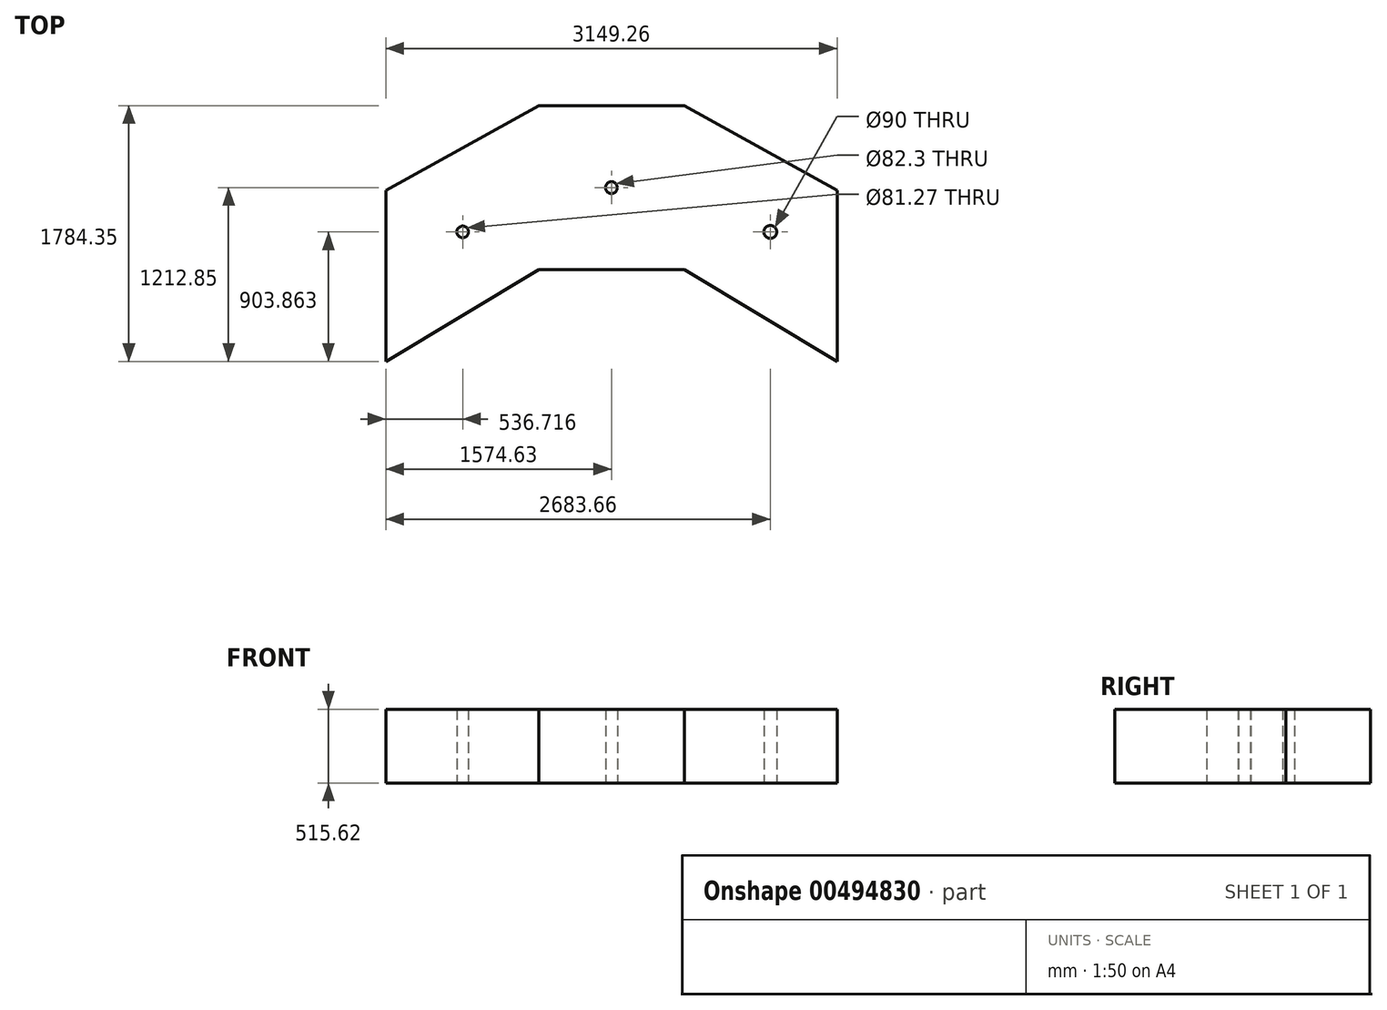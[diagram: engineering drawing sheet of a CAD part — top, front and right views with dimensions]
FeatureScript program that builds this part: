
annotation { "Feature Type Name" : "Feature", "Feature Type Description" : "" }
export const myFeature = defineFeature(function(context is Context, id is Id, definition is map)
    precondition{}
    {
        {
            var Q0;
            Q0=qCreatedBy(makeId("Top.planeOp"),FACE);
            var sketch = newSketch(context, id + "F0", { "sketchPlane" : qUnion([Q0])});
            skLineSegment(sketch, "E0", {"start": v(459.4, 1143) * mm, "end": v(-556.6, 1143) * mm});
            skLineSegment(sketch, "E1", {"start": v(-556.6, 1143) * mm, "end": v(-1623.22, 552.45) * mm});
            skLineSegment(sketch, "E2", {"start": v(-1623.22, 552.45) * mm, "end": v(-1623.22, -641.35) * mm});
            skLineSegment(sketch, "E3", {"start": v(-1623.22, -641.35) * mm, "end": v(-556.6, 0) * mm});
            skLineSegment(sketch, "E4", {"start": v(-556.6, 0) * mm, "end": v(459.4, 0) * mm});
            skLineSegment(sketch, "E5", {"start": v(459.4, 0) * mm, "end": v(1526.04, -641.35) * mm});
            skLineSegment(sketch, "E6", {"start": v(1526.04, -641.35) * mm, "end": v(1526.04, 552.45) * mm});
            skLineSegment(sketch, "E7", {"start": v(1526.04, 552.45) * mm, "end": v(459.4, 1143) * mm});
            skLineSegment(sketch, "E8", {"start": v(-556.6, 1143) * mm, "end": v(-556.6, 0) * mm});
            skLineSegment(sketch, "E9", {"start": v(459.4, 1143) * mm, "end": v(459.4, 0) * mm});
            skCircle(sketch, "E10", {"center": v(-48.6, 571.5) * mm, "radius": 41.15 * mm});
            skCircle(sketch, "E11", {"center": v(-48.6, 571.5) * mm, "radius": 36.25 * mm});
            skCircle(sketch, "E12", {"center": v(-1086.5, 262.51) * mm, "radius": 36.39 * mm});
            skCircle(sketch, "E13", {"center": v(-1086.5, 262.51) * mm, "radius": 40.63 * mm});
            skCircle(sketch, "E14", {"center": v(1060.44, 262.51) * mm, "radius": 40.63 * mm});
            skCircle(sketch, "E15", {"center": v(1060.44, 262.51) * mm, "radius": 45 * mm});
            skSolve(sketch);
        }
        {
            var Q0;
            Q0=makeQuery(id+"F0.imprint","IMPRINT",FACE,{"disambiguationData":[TD([[makeQuery(id+"F0.imprint","IMPRINT",EDGE,{"derivedFrom":sQuery(id+"F0.wireOp",EDGE,"E0")}),1.0]])]});
            var Q1;
            Q1=makeQuery(id+"F0.imprint","IMPRINT",FACE,{"disambiguationData":[TD([[makeQuery(id+"F0.imprint","IMPRINT",EDGE,{"derivedFrom":sQuery(id+"F0.wireOp",EDGE,"E1")}),1.0]])]});
            var Q2;
            Q2=makeQuery(id+"F0.imprint","IMPRINT",FACE,{"disambiguationData":[TD([[makeQuery(id+"F0.imprint","IMPRINT",EDGE,{"derivedFrom":sQuery(id+"F0.wireOp",EDGE,"E5")}),1.0]])]});
            extrude(context, id + "F1", {"entities" : qUnion([Q0, Q1, Q2]), "depth" : 515.62 * mm});
        }
    });
